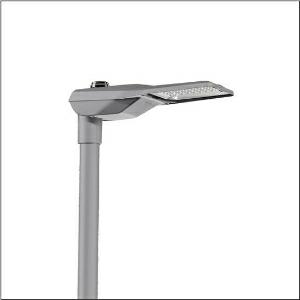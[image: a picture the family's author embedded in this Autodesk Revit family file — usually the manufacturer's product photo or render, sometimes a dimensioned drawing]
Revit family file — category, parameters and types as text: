
# Revit family: streetlight_sl_21_mini___st0_5a_5xe6b47n08gb_d394
name_source: partatom
category: Lighting Fixtures
units: mm (PartAtom-declared; Revit-internal decimal feet)

## family parameters
Cut with Voids When Loaded = No
Host = Face
Light Source = No
Part Type = Normal
Room Calculation Point = No
Round Connector Dimension = Use Diameter
Shared = No

## types (1)
- --- (1 x LED, 6180 lm, 40.4 W, 4000K)
    Apparent Load = 40 VA
    CIE Flux Codes = 41 75 97 100 100
    Color Rendering = 70
    Color Temperature = 4000K
    Default Elevation = 1800 mm
    Description = Streetlight SL 21 mini, mast luminaire, primary light control with lens, of PMMA, primary optical cover: cover, of toughened safety glass, transparent, light distribution: ST0.5a, light emission: direct distribution, primary light characteristic: asymmetric, installation type: side-entry, LED, 3G 1.5mm², High Power LED, rated luminous flux: 6.180lm, luminous efficacy: 153lm/W, light colour: 740, colour temperature: 4000K, control gear: NEMA (7pin), control: overheat protection, pre-setting: linear dimming characteristic, constant luminous flux control, time-dependent luminous flux control, flexible luminous flux parameterisation, mains connection: 230..240V, AC, 50/60Hz, connection cable pre-assembled, cable length: 8,5m, wiring characteristics: H07RN-F, start of lifetime: 40W, end of service life: 41W, reduction: 19W, luminaire housing, of diecast aluminium (EN AC-44300), powder-coated, SITECO metallic grey (DB 702S), corrosivity category C5 high according to DIN EN ISO 12944, multi-level sealing system, sealing non-destructively replaceable, inclination adjustable: 0°, 5°, 10°, 15°, length: 628mm, width: 235mm, height: 110mm, spigot size: 42mm (side-entry), mounting height: 4..8m, protection rating (complete): IP66, insulation class (complete): insulation class I (protective earthing), certification: CE, ENEC, ENEC+, VDE, impact resistance: IK10, permissible operating ambient temperature for outdoor applications: -40..+50°C, standard-compliant lighting for roads and squares, packaging unit: 1 piece

Light Distribution: ST0.5a
    Height = 110 mm
    Lamp = 1 x LED
    Lamp Light Flux = 6180 lm
    Lamp Power = 40.4 W
    Lamp count = 1
    Length = 625 mm
    Luminous efficacy = 153 lm/W
    Manufacturer = Siteco
    ModVariant = No
    Model = 5XE6B47N08GB
    Number of Poles = 1
    OnlyDefault = Yes
    Power Factor = 1
    Product Name = Streetlight SL 21 mini | ST0.5a
    Product group = mast luminaire | pylon top
    ProductGroupID = 6100
    Protection Class = Protection class I
    Protection Degree = IP 66
    RLX_Detail_Level = 1
    RLX_Emergency_Light_Flux = 0 lm
    RLX_Emergency_Type = 0
    RLX_Emergency_Type_DB = No
    RlxData = <blob elided: 36841 chars, md5=3d3f4763>
    Socket = socket
    Standby Power = 0 W
    System Light Flux = 6180 lm
    System Power = 40 W
    Type Comments = factory setting: luminous flux: 100 % | dim-lin: 254 | 812 mA
    Type Image = l_1294379.jpg
    URL = http://relux.com
    VarID = @adj_136953
    Voltage = 0 V
    Weight = 0.00 kg
    Width = 234 mm

## geometry (parser evidence)
native form markers: Blend x4, Sweep x10
no freeform markers — native parametric forms only
